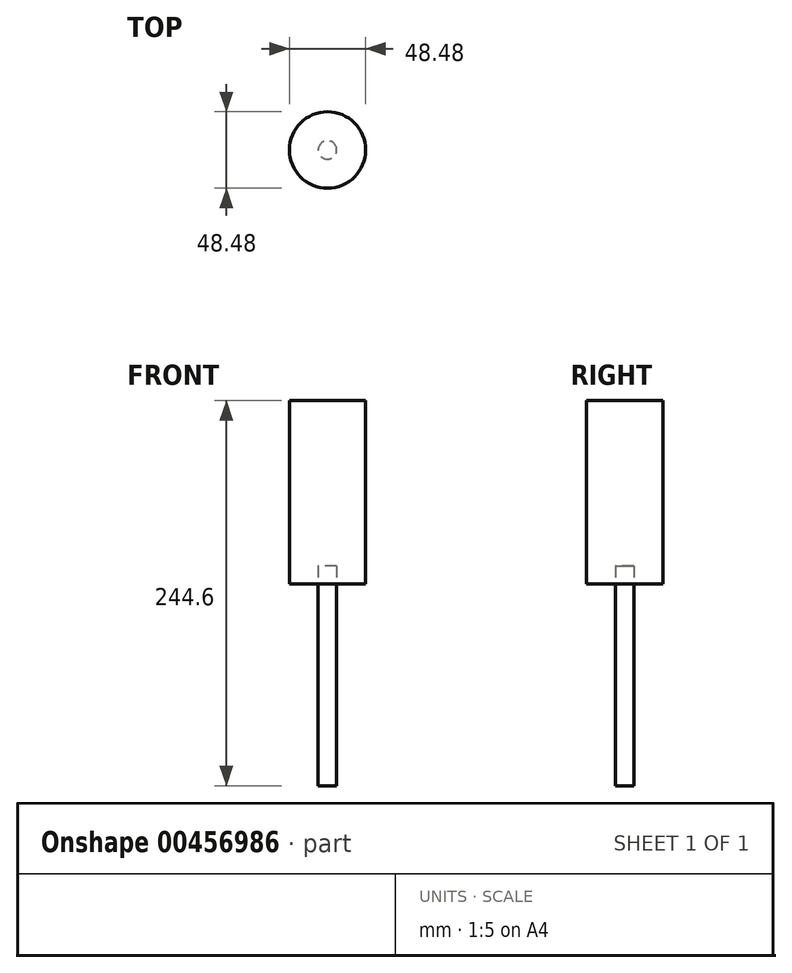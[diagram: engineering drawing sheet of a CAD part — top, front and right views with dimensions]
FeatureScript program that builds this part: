
annotation { "Feature Type Name" : "Feature", "Feature Type Description" : "" }
export const myFeature = defineFeature(function(context is Context, id is Id, definition is map)
    precondition{}
    {
        {
            var Q0;
            Q0=qCreatedBy(makeId("Top.planeOp"),FACE);
            var sketch = newSketch(context, id + "F0", { "sketchPlane" : qUnion([Q0])});
            skCircle(sketch, "E0", {"center": v(0, 0) * mm, "radius": 5.89 * mm});
            skSolve(sketch);
        }
        {
            var Q0;
            Q0=makeQuery(id+"F0.imprint","IMPRINT",FACE,{"disambiguationData":[TD([[makeQuery(id+"F0.imprint","IMPRINT",EDGE,{"derivedFrom":sQuery(id+"F0.wireOp",EDGE,"E0")}),1.0]])]});
            extrude(context, id + "F1", {"entities" : qUnion([Q0]), "depth" : 139.7 * mm});
        }
        {
            var Q0;
            Q0=qCreatedBy(makeId("Top.planeOp"),FACE);
            var sketch = newSketch(context, id + "F2", { "sketchPlane" : qUnion([Q0])});
            skCircle(sketch, "E1", {"center": v(0, 0) * mm, "radius": 24.24 * mm});
            skSolve(sketch);
        }
        {
            var Q0;
            Q0=makeQuery(id+"F2.imprint","IMPRINT",FACE,{"disambiguationData":[TD([[makeQuery(id+"F2.imprint","IMPRINT",EDGE,{"derivedFrom":sQuery(id+"F2.wireOp",EDGE,"E1")}),1.0]])]});
            extrude(context, id + "F3", {"entities" : qUnion([Q0]), "depth" : 116.33 * mm});
        }
        {
            var Q0;
            Q0=makeQuery(id+"F3.opExtrude","SWEPT_BODY",BODY,{"disambiguationData":[OSD([sQuery(id+"F2.wireOp",EDGE,"E1")])]});
            var Q1;
            Q1=makeQuery(id+"F1.opExtrude","CAP_EDGE",EDGE,{"disambiguationData":[OSD([sQuery(id+"F0.wireOp",EDGE,"E0")])],"isStart":false});
            transform(context, id + "F4", {"entities" : qUnion([Q0]), "transformType" : TransformType.TRANSLATION_3D, "dx" : 0 * mm, "dy" : 0 * mm, "dz" : 145.29 * mm, "makeCopy" : false});
        }
        {
            var Q0;
            Q0=makeQuery(id+"F3.opExtrude","SWEPT_BODY",BODY,{"disambiguationData":[OSD([sQuery(id+"F2.wireOp",EDGE,"E1")])]});
            transform(context, id + "F5", {"entities" : qUnion([Q0]), "transformType" : TransformType.TRANSLATION_3D, "dx" : 0 * mm, "dy" : 0 * mm, "dz" : -17.02 * mm, "makeCopy" : false});
        }
    });
